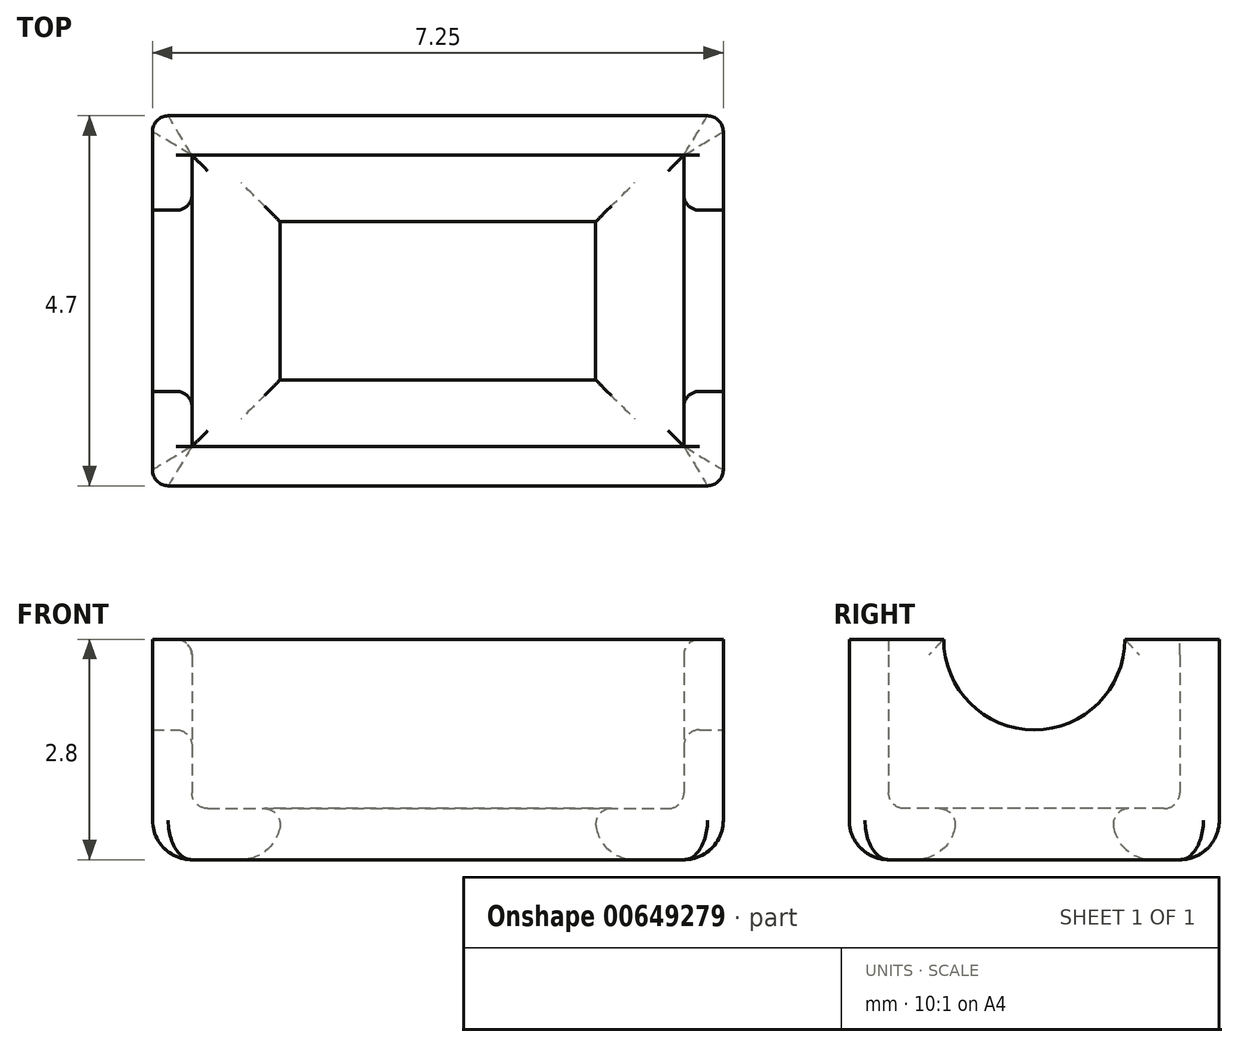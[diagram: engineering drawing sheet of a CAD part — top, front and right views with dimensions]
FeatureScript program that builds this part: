
annotation { "Feature Type Name" : "Feature", "Feature Type Description" : "" }
export const myFeature = defineFeature(function(context is Context, id is Id, definition is map)
    precondition{}
    {
        {
            var Q0;
            Q0=qCreatedBy(makeId("Top.planeOp"),FACE);
            var sketch = newSketch(context, id + "F0", { "sketchPlane" : qUnion([Q0])});
            skLineSegment(sketch, "E0.bottom", {"start": v(-10.65, -2.65) * mm, "end": v(-4.4, -2.65) * mm});
            skLineSegment(sketch, "E0.top", {"start": v(-10.65, -6.35) * mm, "end": v(-4.4, -6.35) * mm});
            skLineSegment(sketch, "E0.left", {"start": v(-10.65, -2.65) * mm, "end": v(-10.65, -6.35) * mm});
            skLineSegment(sketch, "E0.right", {"start": v(-4.4, -2.65) * mm, "end": v(-4.4, -6.35) * mm});
            skLineSegment(sketch, "E1.bottom", {"start": v(-9.52, -3.5) * mm, "end": v(-5.52, -3.5) * mm});
            skLineSegment(sketch, "E1.top", {"start": v(-9.52, -5.5) * mm, "end": v(-5.52, -5.5) * mm});
            skLineSegment(sketch, "E1.left", {"start": v(-9.52, -3.5) * mm, "end": v(-9.52, -5.5) * mm});
            skLineSegment(sketch, "E1.right", {"start": v(-5.52, -3.5) * mm, "end": v(-5.52, -5.5) * mm});
            skLineSegment(sketch, "E2.0", {"start": v(-11.15, -6.85) * mm, "end": v(-3.9, -6.85) * mm});
            skLineSegment(sketch, "E2.1", {"start": v(-11.15, -2.15) * mm, "end": v(-11.15, -6.85) * mm});
            skLineSegment(sketch, "E2.2", {"start": v(-11.15, -2.15) * mm, "end": v(-3.9, -2.15) * mm});
            skLineSegment(sketch, "E2.3", {"start": v(-3.9, -2.15) * mm, "end": v(-3.9, -6.85) * mm});
            skSolve(sketch);
        }
        {
            var Q0;
            Q0=makeQuery(id+"F0.imprint","IMPRINT",FACE,{"disambiguationData":[TD([[makeQuery(id+"F0.imprint","IMPRINT",EDGE,{"derivedFrom":sQuery(id+"F0.wireOp",EDGE,"E0.bottom")}),1.0]])]});
            extrude(context, id + "F1", {"entities" : qUnion([Q0]), "depth" : 2.8 * mm, "offsetDistance" : 25 * mm});
        }
        {
            var Q0;
            Q0=makeQuery(id+"F0.imprint","IMPRINT",FACE,{"disambiguationData":[TD([[makeQuery(id+"F0.imprint","IMPRINT",EDGE,{"derivedFrom":sQuery(id+"F0.wireOp",EDGE,"E0.bottom")}),-1.0]])]});
            extrude(context, id + "F2", {"entities" : qUnion([Q0]), "operationType" : NewBodyOperationType.ADD, "depth" : 0.65 * mm, "offsetDistance" : 25 * mm});
        }
        {
            var Q0;
            {var subQ0=sQuery(id+"F0.wireOp",EDGE,"E0.right");var subQ1=sQuery(id+"F0.wireOp",EDGE,"E0.left");var subQ2=sQuery(id+"F0.wireOp",EDGE,"E0.top");var subQ3=sQuery(id+"F0.wireOp",EDGE,"E0.bottom");Q0=makeQuery(id+"F2.boolean.opBoolean","MERGE",FACE,{"derivedFrom":[makeQuery(id+"F1.opExtrude","CAP_FACE",FACE,{"disambiguationData":[OSD([subQ3,subQ2,subQ1,subQ0,sQuery(id+"F0.wireOp",EDGE,"E2.0"),sQuery(id+"F0.wireOp",EDGE,"E2.1"),sQuery(id+"F0.wireOp",EDGE,"E2.2"),sQuery(id+"F0.wireOp",EDGE,"E2.3")])],"isStart":true}),makeQuery(id+"F2.opExtrude","CAP_FACE",FACE,{"disambiguationData":[OSD([subQ3,subQ2,subQ1,subQ0,sQuery(id+"F0.wireOp",EDGE,"E1.bottom"),sQuery(id+"F0.wireOp",EDGE,"E1.top"),sQuery(id+"F0.wireOp",EDGE,"E1.left"),sQuery(id+"F0.wireOp",EDGE,"E1.right")])],"isStart":true})]});}
            fillet(context, id + "F3", {"entities" : qUnion([Q0]), "radius" : 0.5 * mm, "tangentPropagation" : true, "allowEdgeOverflow" : false});
        }
        {
            var Q0;
            Q0=makeQuery(id+"F1.opExtrude","SWEPT_FACE",FACE,{"disambiguationData":[OSD([sQuery(id+"F0.wireOp",EDGE,"E2.3")])]});
            var sketch = newSketch(context, id + "F4", { "sketchPlane" : qUnion([Q0])});
            skCircle(sketch, "E3", {"center": v(-4.5, 2.8) * mm, "radius": 1.15 * mm});
            skSolve(sketch);
        }
        {
            var Q0;
            {var subQ0=sQuery(id+"F4.wireOp",EDGE,"E3");var subQ1=makeQuery(id+"F1.opExtrude","CAP_EDGE",EDGE,{"disambiguationData":[OSD([sQuery(id+"F0.wireOp",EDGE,"E2.3")])],"isStart":false});var subQ2=makeQuery(id+"F4.imprint","INTERSECT",VERTEX,{"disambiguationData":[OD(0.0)],"derivedFrom":[subQ1,subQ0]});Q0=makeQuery(id+"F4.imprint","IMPRINT",FACE,{"disambiguationData":[TD([[makeQuery(id+"F4.imprint","IMPRINT",EDGE,{"disambiguationData":[TD([[subQ2,-1.0]])],"derivedFrom":subQ0}),1.0]])]});}
            extrude(context, id + "F5", {"entities" : qUnion([Q0]), "operationType" : NewBodyOperationType.REMOVE, "oppositeDirection" : true, "depth" : 25 * mm, "offsetDistance" : 25 * mm});
        }
        {
            var Q0;
            Q0=makeQuery(id+"F2.opExtrude","CAP_FACE",FACE,{"disambiguationData":[OSD([sQuery(id+"F0.wireOp",EDGE,"E0.bottom"),sQuery(id+"F0.wireOp",EDGE,"E0.top"),sQuery(id+"F0.wireOp",EDGE,"E0.left"),sQuery(id+"F0.wireOp",EDGE,"E0.right"),sQuery(id+"F0.wireOp",EDGE,"E1.bottom"),sQuery(id+"F0.wireOp",EDGE,"E1.top"),sQuery(id+"F0.wireOp",EDGE,"E1.left"),sQuery(id+"F0.wireOp",EDGE,"E1.right")])],"isStart":false});
            var Q1;
            Q1=makeQuery(id+"F5.boolean.opBoolean","INTERSECT",EDGE,{"derivedFrom":[makeQuery(id+"F1.opExtrude","SWEPT_FACE",FACE,{"disambiguationData":[OSD([sQuery(id+"F0.wireOp",EDGE,"E0.left")])]}),makeQuery(id+"F5.opExtrude","SWEPT_FACE",FACE,{"disambiguationData":[OSD([sQuery(id+"F4.wireOp",EDGE,"E3")])]})]});
            var Q2;
            Q2=makeQuery(id+"F5.boolean.opBoolean","INTERSECT",EDGE,{"derivedFrom":[makeQuery(id+"F1.opExtrude","SWEPT_FACE",FACE,{"disambiguationData":[OSD([sQuery(id+"F0.wireOp",EDGE,"E0.right")])]}),makeQuery(id+"F5.opExtrude","SWEPT_FACE",FACE,{"disambiguationData":[OSD([sQuery(id+"F4.wireOp",EDGE,"E3")])]})]});
            var Q3;
            {var subQ0=sQuery(id+"F0.wireOp",EDGE,"E0.bottom");var subQ1=sQuery(id+"F0.wireOp",EDGE,"E0.left");Q3=makeQuery(id+"F5.boolean.opBoolean","SPLIT",EDGE,{"disambiguationData":[TD([makeQuery(id+"F1.opExtrude","SWEPT_FACE",FACE,{"disambiguationData":[OSD([subQ0])]})])],"derivedFrom":makeQuery(id+"F1.opExtrude","CAP_EDGE",EDGE,{"disambiguationData":[OSD([subQ1])],"isStart":false})});}
            var Q4;
            Q4=makeQuery(id+"F1.opExtrude","SWEPT_EDGE",EDGE,{"disambiguationData":[OSD([sQuery(id+"F0.wireOp",EDGE,"E2.2"),sQuery(id+"F0.wireOp",EDGE,"E2.3")])]});
            var Q5;
            Q5=makeQuery(id+"F1.opExtrude","SWEPT_EDGE",EDGE,{"disambiguationData":[OSD([sQuery(id+"F0.wireOp",EDGE,"E2.0"),sQuery(id+"F0.wireOp",EDGE,"E2.3")])]});
            var Q6;
            Q6=makeQuery(id+"F1.opExtrude","SWEPT_EDGE",EDGE,{"disambiguationData":[OSD([sQuery(id+"F0.wireOp",EDGE,"E2.1"),sQuery(id+"F0.wireOp",EDGE,"E2.2")])]});
            var Q7;
            Q7=makeQuery(id+"F1.opExtrude","SWEPT_EDGE",EDGE,{"disambiguationData":[OSD([sQuery(id+"F0.wireOp",EDGE,"E2.0"),sQuery(id+"F0.wireOp",EDGE,"E2.1")])]});
            var Q8;
            {var subQ0=sQuery(id+"F0.wireOp",EDGE,"E0.bottom");var subQ1=sQuery(id+"F0.wireOp",EDGE,"E0.right");Q8=makeQuery(id+"F5.boolean.opBoolean","SPLIT",EDGE,{"disambiguationData":[TD([makeQuery(id+"F1.opExtrude","SWEPT_FACE",FACE,{"disambiguationData":[OSD([subQ0])]})])],"derivedFrom":makeQuery(id+"F1.opExtrude","CAP_EDGE",EDGE,{"disambiguationData":[OSD([subQ1])],"isStart":false})});}
            var Q9;
            {var subQ0=sQuery(id+"F0.wireOp",EDGE,"E0.right");var subQ1=sQuery(id+"F0.wireOp",EDGE,"E0.top");Q9=makeQuery(id+"F5.boolean.opBoolean","SPLIT",EDGE,{"disambiguationData":[TD([makeQuery(id+"F1.opExtrude","SWEPT_FACE",FACE,{"disambiguationData":[OSD([subQ1])]})])],"derivedFrom":makeQuery(id+"F1.opExtrude","CAP_EDGE",EDGE,{"disambiguationData":[OSD([subQ0])],"isStart":false})});}
            var Q10;
            {var subQ0=sQuery(id+"F0.wireOp",EDGE,"E0.left");var subQ1=sQuery(id+"F0.wireOp",EDGE,"E0.top");Q10=makeQuery(id+"F5.boolean.opBoolean","SPLIT",EDGE,{"disambiguationData":[TD([makeQuery(id+"F1.opExtrude","SWEPT_FACE",FACE,{"disambiguationData":[OSD([subQ1])]})])],"derivedFrom":makeQuery(id+"F1.opExtrude","CAP_EDGE",EDGE,{"disambiguationData":[OSD([subQ0])],"isStart":false})});}
            fillet(context, id + "F6", {"entities" : qUnion([Q0, Q1, Q2, Q3, Q4, Q5, Q6, Q7, Q8, Q9, Q10]), "radius" : 0.2 * mm, "tangentPropagation" : true, "allowEdgeOverflow" : false});
        }
    });
